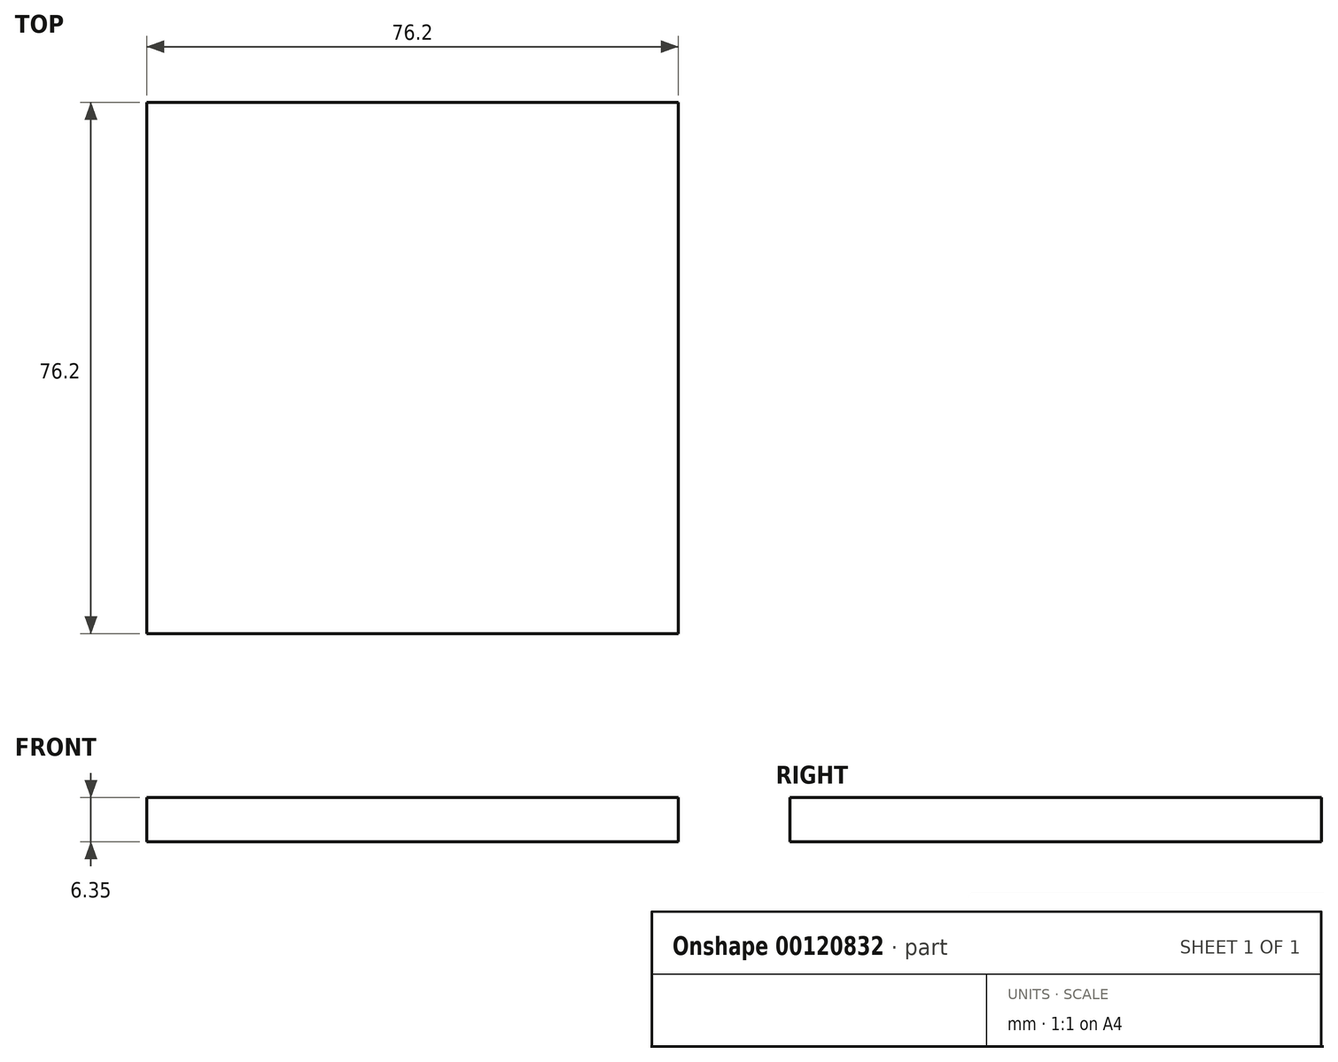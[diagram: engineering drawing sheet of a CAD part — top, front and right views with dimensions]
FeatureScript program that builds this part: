
annotation { "Feature Type Name" : "Feature", "Feature Type Description" : "" }
export const myFeature = defineFeature(function(context is Context, id is Id, definition is map)
    precondition{}
    {
        {
            var Q0;
            Q0=qCreatedBy(makeId("Top.planeOp"),FACE);
            var sketch = newSketch(context, id + "F0", { "sketchPlane" : qUnion([Q0])});
            skLineSegment(sketch, "E0.bottom", {"start": v(-42.79, -44.23) * mm, "end": v(33.41, -44.23) * mm});
            skLineSegment(sketch, "E0.top", {"start": v(-42.79, 31.97) * mm, "end": v(33.41, 31.97) * mm});
            skLineSegment(sketch, "E0.left", {"start": v(-42.79, -44.23) * mm, "end": v(-42.79, 31.97) * mm});
            skLineSegment(sketch, "E0.right", {"start": v(33.41, -44.23) * mm, "end": v(33.41, 31.97) * mm});
            skSolve(sketch);
        }
        {
            var Q0;
            Q0 = qSketchRegion(id + "F0", true);
            extrude(context, id + "F1", {"entities" : qUnion([Q0]), "depth" : 6.35 * mm});
        }
    });
